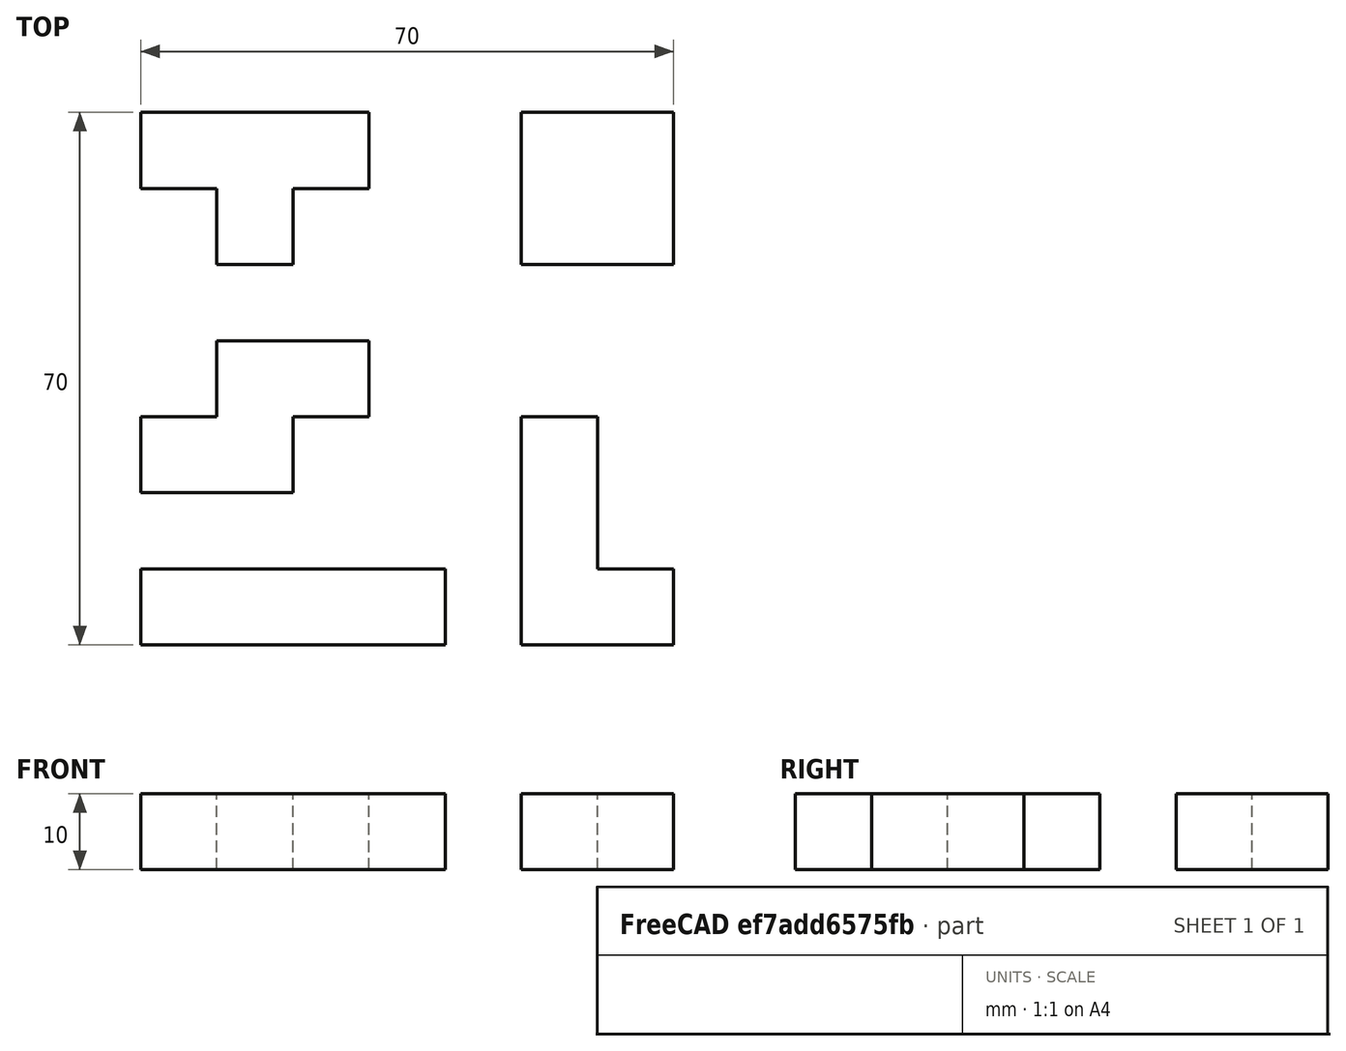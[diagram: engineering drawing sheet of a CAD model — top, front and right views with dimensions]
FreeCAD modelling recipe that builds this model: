
FCSTD DOCUMENT  (FreeCAD 0.21R33771 (Git))
Label: OJT1_T05R03_unions_tetris_v2
License: All rights reserved
LicenseURL: http://en.wikipedia.org/wiki/All_rights_reserved
objects: Part::Box×20, Part::MultiFuse×5
note: 25 computed .brp shape members not serialized (recipe doc carries the construction recipe); baked Part::Feature solids carry a one-line shape summary decoded from their .brp

FEATURE [Part::Box] Box  label="Cube"
  AttacherType = Attacher::AttachEngine3D
  Height = 10
  Length = 10
  Width = 10
FEATURE [Part::Box] Box001  label="Cube001"
  AttacherType = Attacher::AttachEngine3D
  Height = 10
  Length = 10
  Placement = pos=(10,0,0) rot=(0,0,1;0rad)
  Width = 10
FEATURE [Part::Box] Box002  label="Cube002"
  AttacherType = Attacher::AttachEngine3D
  Height = 10
  Length = 10
  Placement = pos=(20,0,0) rot=(0,0,1;0rad)
  Width = 10
FEATURE [Part::Box] Box003  label="Cube003"
  AttacherType = Attacher::AttachEngine3D
  Height = 10
  Length = 10
  Placement = pos=(30,0,0) rot=(0,0,1;0rad)
  Width = 10
FEATURE [Part::MultiFuse] Fusion  label="vermell"
  Refine = true
  Shapes = -> [Box003,Box,Box001,Box002]
FEATURE [Part::Box] Box004  label="Cube004"
  AttacherType = Attacher::AttachEngine3D
  Height = 10
  Length = 10
  Placement = pos=(50,0,0) rot=(0,0,1;0rad)
  Width = 10
FEATURE [Part::Box] Box005  label="Cube005"
  AttacherType = Attacher::AttachEngine3D
  Height = 10
  Length = 10
  Placement = pos=(60,0,0) rot=(0,0,1;0rad)
  Width = 10
FEATURE [Part::Box] Box006  label="Cube006"
  AttacherType = Attacher::AttachEngine3D
  Height = 10
  Length = 10
  Placement = pos=(50,10,0) rot=(0,0,1;0rad)
  Width = 10
FEATURE [Part::Box] Box007  label="Cube007"
  AttacherType = Attacher::AttachEngine3D
  Height = 10
  Length = 10
  Placement = pos=(50,20,0) rot=(0,0,1;0rad)
  Width = 10
FEATURE [Part::MultiFuse] Fusion001  label="groc"
  Refine = true
  Shapes = -> [Box007,Box004,Box005,Box006]
FEATURE [Part::Box] Box008  label="Cube008"
  AttacherType = Attacher::AttachEngine3D
  Height = 10
  Length = 10
  Placement = pos=(0,20,0) rot=(0,0,1;0rad)
  Width = 10
FEATURE [Part::Box] Box009  label="Cube009"
  AttacherType = Attacher::AttachEngine3D
  Height = 10
  Length = 10
  Placement = pos=(10,20,0) rot=(0,0,1;0rad)
  Width = 10
FEATURE [Part::Box] Box010  label="Cube010"
  AttacherType = Attacher::AttachEngine3D
  Height = 10
  Length = 10
  Placement = pos=(10,30,0) rot=(0,0,1;0rad)
  Width = 10
FEATURE [Part::Box] Box011  label="Cube011"
  AttacherType = Attacher::AttachEngine3D
  Height = 10
  Length = 10
  Placement = pos=(20,30,0) rot=(0,0,1;0rad)
  Width = 10
FEATURE [Part::MultiFuse] Fusion002  label="blau"
  Refine = true
  Shapes = -> [Box008,Box009,Box010,Box011]
FEATURE [Part::Box] Box012  label="Cube012"
  AttacherType = Attacher::AttachEngine3D
  Height = 10
  Length = 10
  Placement = pos=(10,50,0) rot=(0,0,1;0rad)
  Width = 10
FEATURE [Part::Box] Box013  label="Cube013"
  AttacherType = Attacher::AttachEngine3D
  Height = 10
  Length = 10
  Placement = pos=(0,60,0) rot=(0,0,1;0rad)
  Width = 10
FEATURE [Part::Box] Box014  label="Cube014"
  AttacherType = Attacher::AttachEngine3D
  Height = 10
  Length = 10
  Placement = pos=(10,60,0) rot=(0,0,1;0rad)
  Width = 10
FEATURE [Part::Box] Box015  label="Cube015"
  AttacherType = Attacher::AttachEngine3D
  Height = 10
  Length = 10
  Placement = pos=(20,60,0) rot=(0,0,1;0rad)
  Width = 10
FEATURE [Part::MultiFuse] Fusion003  label="gris"
  Refine = true
  Shapes = -> [Box012,Box013,Box014,Box015]
FEATURE [Part::Box] Box016  label="Cube016"
  AttacherType = Attacher::AttachEngine3D
  Height = 10
  Length = 10
  Placement = pos=(50,60,0) rot=(0,0,1;0rad)
  Width = 10
FEATURE [Part::Box] Box017  label="Cube017"
  AttacherType = Attacher::AttachEngine3D
  Height = 10
  Length = 10
  Placement = pos=(50,50,0) rot=(0,0,1;0rad)
  Width = 10
FEATURE [Part::Box] Box018  label="Cube018"
  AttacherType = Attacher::AttachEngine3D
  Height = 10
  Length = 10
  Placement = pos=(60,60,0) rot=(0,0,1;0rad)
  Width = 10
FEATURE [Part::Box] Box019  label="Cube019"
  AttacherType = Attacher::AttachEngine3D
  Height = 10
  Length = 10
  Placement = pos=(60,50,0) rot=(0,0,1;0rad)
  Width = 10
FEATURE [Part::MultiFuse] Fusion004  label="blau_cel"
  Refine = true
  Shapes = -> [Box016,Box017,Box018,Box019]
